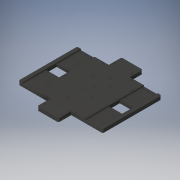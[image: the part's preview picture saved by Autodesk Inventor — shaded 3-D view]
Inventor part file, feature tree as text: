
AUTODESK INVENTOR PART (.ipt)
format: ipt  version: 2017 (Build 210142000, 142)  size: 471,040 bytes
history: native  units: in
note: dims shown in document units (in); Inventor stores cm internally (conversion verified against a paired STEP export)
features: extrude x10, sketch x10, projected_geometry x10, fillet x1
ambient origin geometry x8: Origin, YZ Plane, XZ Plane, XY Plane, X Axis, Y Axis, Z Axis, Center Point
bodies: Solid1 (feature_tree)
feature tree (31):
  extrude  "Extrusion1"  Depth=9.0in
  extrude  "Extrusion2"  Depth=1.118in
  extrude  "Extrusion3"  Depth=0.25in
  extrude  "Extrusion4"  TaperAngle=0.0deg  [1 undecoded]
  extrude  "Extrusion5"  Depth=0.375in
  extrude  "Extrusion7"  Depth=0.125in
  extrude  "ardMount"  Depth=0.125in TaperAngle=0.0deg
  extrude  "piMount"  Depth=0.125in TaperAngle=0.0deg
  extrude  "sabertoothMount"  Depth=3.0in
  extrude  "Extrusion11"  Depth=0.125in TaperAngle=0.0deg
  fillet  "Fillet1"  Radius=1.368in
  sketch  "Sketch1"  dims[d0=9.0in d1=9.0in]
  sketch  "Sketch2"  dims[d2=2.3622in d3=1.118in]
  projected_geometry  "Projected Loop1"
  sketch  "Sketch3"  dims[d4=0.375in d5=0.0in d6=0.25in]
  projected_geometry  "Projected Loop2"
  projected_geometry  "Projected Loop3"
  projected_geometry  "Projected Loop4"
  projected_geometry  "Projected Loop5"
  sketch  "Sketch4"  dims[d7=0.375in d8=0.0in]
  sketch  "Sketch5"  dims[d9=1.5in d10=0.375in]
  sketch  "Sketch7"  dims[d11=0.125in d12=0.5827in]
  projected_geometry  "Projected Loop7"
  sketch  "Sketch8"  dims[d13=0.125in d14=0.0312in d15=0.0in]
  projected_geometry  "Projected Loop8"
  sketch  "Sketch9"  dims[d16=0.125in d17=0.0in d18=0.125in d19=0.0in]
  projected_geometry  "Projected Loop9"
  sketch  "Sketch10"  dims[d20=1.5in d21=3.0in]
  projected_geometry  "Projected Loop10"
  sketch  "Sketch11"  dims[d22=0.125in d23=0.125in d24=0.0in d30=1.368in d31=1.0in d32=0.0in d33=0.172in d34=3.543in d35=0.63in d36=0.172in d37=0.571in d38=3.799in d39=0.125in d40=0.125in d41=0.125in d42=0.125in d43=1.0in d44=0.0in d45=0.161in d46=0.93in d47=3.21in d48=0.125in d49=0.125in d50=1.0in d51=0.0in d52=2.026in d53=2.86in d54=1.12in d55=4.275in d56=2.026in d57=2.86in d58=1.12in d59=4.275in d60=0.125in d61=0.125in d62=0.125in d63=0.125in d64=0.125in d65=0.125in d66=0.125in d67=0.125in d68=1.0in d69=0.0in d70=1.125in d71=1.0in d72=0.0in d73=0.125in d74=0.172in]
  projected_geometry  "Projected Loop11"
note: 1 required parameter value undecoded (feature->parameter linkage not recoverable at this tier; creation-order binding heuristic only, values carry confidence <= 0.55)
